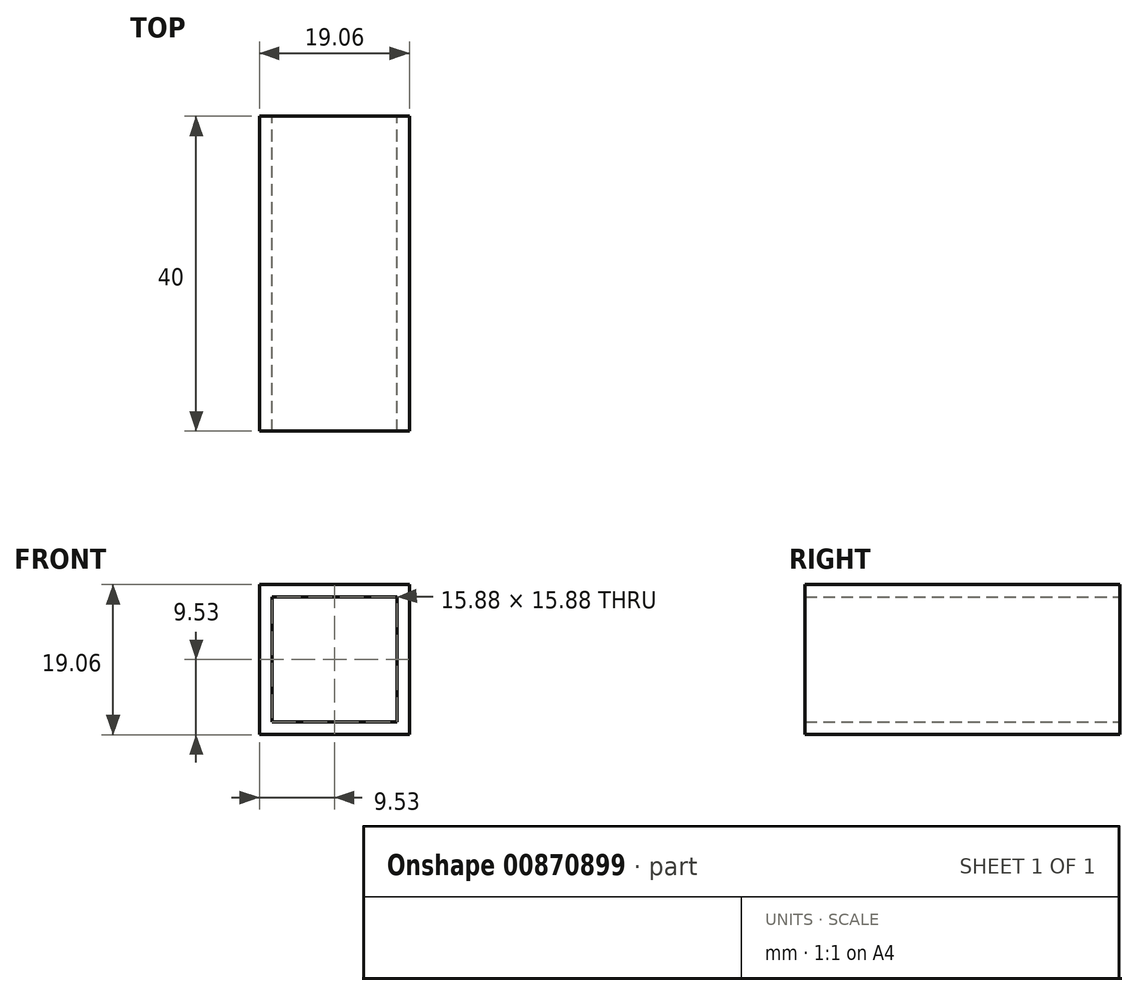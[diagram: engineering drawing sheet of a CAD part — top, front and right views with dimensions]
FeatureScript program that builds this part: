
annotation { "Feature Type Name" : "Feature", "Feature Type Description" : "" }
export const myFeature = defineFeature(function(context is Context, id is Id, definition is map)
    precondition{}
    {
        {
            var Q0;
            Q0=qCreatedBy(makeId("Front.planeOp"),FACE);
            var sketch = newSketch(context, id + "F0", { "sketchPlane" : qUnion([Q0])});
            skLineSegment(sketch, "E0.bottom", {"start": v(9.53, 9.53) * mm, "end": v(-9.53, 9.53) * mm});
            skLineSegment(sketch, "E0.top", {"start": v(9.53, -9.52) * mm, "end": v(-9.53, -9.52) * mm});
            skLineSegment(sketch, "E0.left", {"start": v(9.53, 9.53) * mm, "end": v(9.53, -9.52) * mm});
            skLineSegment(sketch, "E0.right", {"start": v(-9.53, 9.53) * mm, "end": v(-9.53, -9.52) * mm});
            skPoint(sketch, "E0.middle", {"position": v(0, 0) * mm});
            skLineSegment(sketch, "E1.bottom", {"start": v(-7.94, 7.94) * mm, "end": v(7.94, 7.94) * mm});
            skLineSegment(sketch, "E1.top", {"start": v(-7.94, -7.94) * mm, "end": v(7.94, -7.94) * mm});
            skLineSegment(sketch, "E1.left", {"start": v(-7.94, 7.94) * mm, "end": v(-7.94, -7.94) * mm});
            skLineSegment(sketch, "E1.right", {"start": v(7.94, 7.94) * mm, "end": v(7.94, -7.94) * mm});
            skSolve(sketch);
        }
        {
            var Q0;
            Q0=qSketchRegion(id+"F0",true);
            extrude(context, id + "F1", {"entities" : qUnion([Q0]), "depth" : 40 * mm, "offsetDistance" : 25 * mm});
        }
    });
